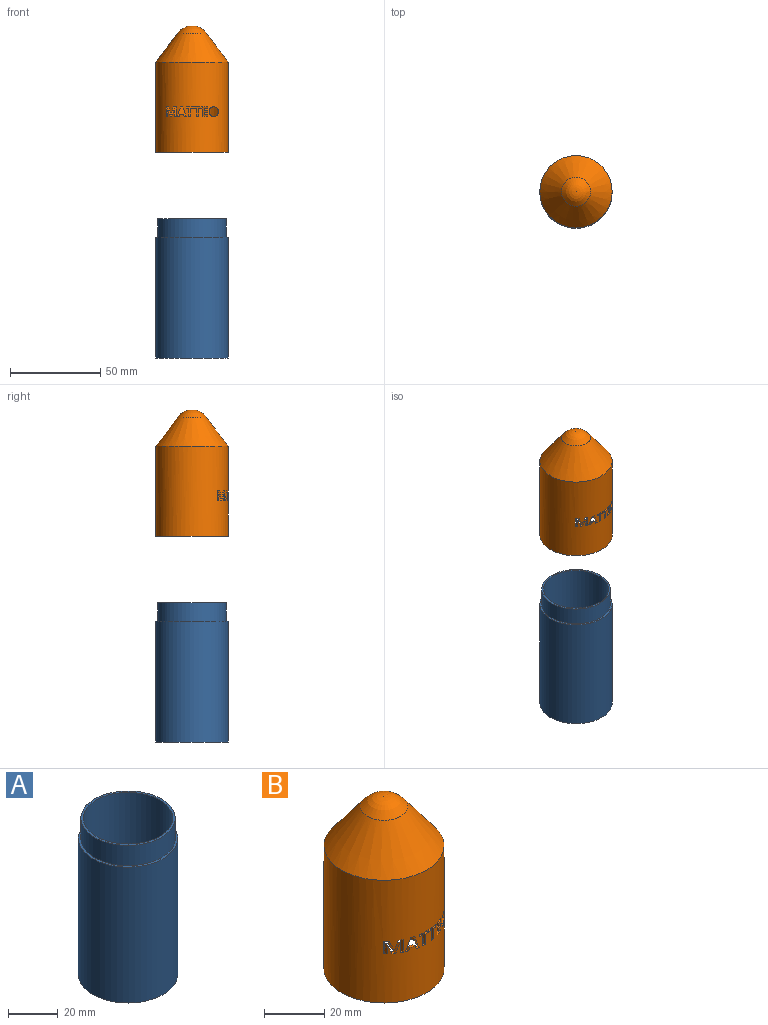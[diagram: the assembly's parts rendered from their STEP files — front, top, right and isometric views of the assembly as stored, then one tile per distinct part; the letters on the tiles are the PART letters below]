
ASSEMBLY  parts=2 mates=1
PART A: 7 faces, bbox 40x40x77 mm
  f0: plane 38x38mm, normal (0,0,1), area 116.2mm2, adj f1,f3
  f1: cylinder r=18mm len=75mm, axis (0,0,-1), area 8482.3mm2, adj f0,f2
  f2: plane 36x36mm, normal (0,0,1), area 1017.9mm2, adj f1
  f3: cylinder r=19mm len=38mm, axis (0,0,1), area 1193.8mm2, adj f0,f4
  f4: plane 40x40mm, normal (0,0,1), area 122.5mm2, adj f3,f6
  f5: plane 40x40mm, normal (0,0,-1), area 1256.6mm2, adj f6
  f6: cylinder r=20mm len=67mm, axis (0,0,-1), area 8419.5mm2, adj f4,f5
PART B: 69 faces, bbox 40x40x70 mm
  f0: cylinder r=19mm len=50mm, axis (0,0,-1), area 5875mm2, adj f2,f3,f6,f7,f8,f9,f10,f11
  f1: cylinder r=20mm len=50mm, axis (0,0,-1), area 6191.1mm2, adj f2,f4,f6,f7,f8,f9,f10,f11
  f2: plane 40x40mm, normal (0,0,-1), area 122.5mm2, adj f0,f1
  f3: plane 38x38mm, normal (0,0,-1), area 1134.1mm2, adj f0
  f4: cone r=20mm half-angle=36.9deg, axis (0,0,-1), area 1759.3mm2, adj f1,f5
  f5: revolved ~16x16mm, area 252.6mm2, adj f4
  f6: extruded ~2.14x1.97mm, area 3.1mm2, adj f0,f1,f7,f13
  f7: extruded ~2.99x1.82mm, area 2.7mm2, adj f0,f1,f6,f8
  f8: extruded ~2.5x1.82mm, area 2.5mm2, adj f0,f1,f7,f9
  f9: extruded ~1.98x1.54mm, area 2.5mm2, adj f0,f1,f8,f10
  f10: extruded ~1.97x1.54mm, area 2.5mm2, adj f0,f1,f9,f11
  f11: extruded ~2.51x1.83mm, area 2.5mm2, adj f0,f1,f10,f12
  f12: extruded ~2.99x1.82mm, area 2.7mm2, adj f0,f1,f11,f13
  f13: extruded ~2.14x1.97mm, area 3.1mm2, adj f0,f1,f6,f12
  f14: plane 4.25x1mm, normal (-1,0,0), area 4.2mm2, adj f0,f1,f15,f21
  f15: plane 1.4x1.02mm, normal (0,0,1), area 1.4mm2, adj f0,f1,f14,f16
  f16: plane 1x0.91mm, normal (-1,0,0), area 0.9mm2, adj f0,f1,f15,f17
  f17: plane 3.89x1.25mm, normal (0,0,-1), area 3.9mm2, adj f0,f1,f16,f18
  f18: plane 1.01x0.91mm, normal (1,0,0), area 0.9mm2, adj f0,f1,f17,f19
  f19: plane 1.4x1.18mm, normal (0,0,1), area 1.4mm2, adj f0,f1,f18,f20
  f20: plane 4.25x1mm, normal (1,0,0), area 4.3mm2, adj f0,f1,f19,f21
  f21: plane 1.09x1.06mm, normal (0,0,1), area 1.1mm2, adj f0,f1,f14,f20
  f22: plane 4.25x1.02mm, normal (-1,0,0), area 4.3mm2, adj f0,f1,f23,f29
  f23: plane 1.4x1.34mm, normal (0,0,1), area 1.4mm2, adj f0,f1,f22,f24
  f24: plane 1.04x0.91mm, normal (-1,0,0), area 0.9mm2, adj f0,f1,f23,f25
  f25: plane 3.89x1.64mm, normal (0,0,-1), area 3.9mm2, adj f0,f1,f24,f26
  f26: plane 1x0.91mm, normal (1,0,0), area 0.9mm2, adj f0,f1,f25,f27
  f27: plane 1.4x1.14mm, normal (0,0,1), area 1.4mm2, adj f0,f1,f26,f28
  f28: plane 4.25x1.01mm, normal (1,0,0), area 4.3mm2, adj f0,f1,f27,f29
  f29: plane 1.19x1.09mm, normal (0,0,1), area 1.1mm2, adj f0,f1,f22,f28
  f30: plane 1.12x0.9mm, normal (-1,0,0), area 1mm2, adj f0,f1,f31,f41
  f31: plane 1.92x1.88mm, normal (0,0,-1), area 2.1mm2, adj f0,f1,f30,f32
  f32: plane 1.33x1.07mm, normal (-1,0,0), area 1.4mm2, adj f0,f1,f31,f33
  f33: plane 1.85x1.75mm, normal (0,0,1), area 1.9mm2, adj f0,f1,f32,f34
  f34: plane 1.12x0.9mm, normal (-1,0,0), area 1mm2, adj f0,f1,f33,f35
  f35: plane 1.85x1.75mm, normal (0,0,-1), area 1.9mm2, adj f0,f1,f34,f36
  f36: plane 1.13x1.07mm, normal (-1,0,0), area 1.2mm2, adj f0,f1,f35,f37
  f37: plane 1.92x1.88mm, normal (0,0,1), area 2.1mm2, adj f0,f1,f36,f38
  f38: plane 1.12x0.9mm, normal (-1,0,0), area 1mm2, adj f0,f1,f37,f39
  f39: plane 2.97x2.29mm, normal (0,0,-1), area 3.2mm2, adj f0,f1,f38,f40
  f40: plane 5.16x1.05mm, normal (1,0,0), area 5.4mm2, adj f0,f1,f39,f41
  f41: plane 2.97x2.29mm, normal (0,0,1), area 3.2mm2, adj f0,f1,f30,f40
  f42: plane 1.23x1.12mm, normal (0.96,0,0.29), area 1.3mm2, adj f0,f1,f43,f49
  f43: plane 1.88x1.62mm, normal (0,0,1), area 2mm2, adj f0,f1,f42,f44
  f44: plane 1.23x1.21mm, normal (-0.96,0,0.29), area 1.4mm2, adj f0,f1,f43,f45
  f45: plane 1.59x1.18mm, normal (0,0,1), area 1.3mm2, adj f0,f1,f44,f46
  f46: plane 5.18x1.82mm, normal (0.94,0,-0.33), area 5.9mm2, adj f0,f1,f45,f47
  f47: plane 1.46x1.34mm, normal (0,0,-1), area 1.4mm2, adj f0,f1,f46,f48
  f48: plane 5.2x1.85mm, normal (-0.94,0,-0.33), area 5.6mm2, adj f0,f1,f47,f49
  f49: plane 1.25x1.18mm, normal (0,0,1), area 1.2mm2, adj f0,f1,f42,f48
  f50: plane 2x1mm, normal (0,0,1), area 1.3mm2, adj f0,f1,f51,f68
  f51: plane 4.04x2.04mm, normal (-0.95,0,0.31), area 5mm2, adj f0,f1,f50,f52
  f52: plane 1.18x0.03mm, normal (0,0,1), area 0mm2, adj f0,f1,f51,f53
  f53: extruded ~1.2x1.19mm, area 1.4mm2, adj f0,f1,f52,f54
  f54: extruded ~1.16x0.4mm, area 0.5mm2, adj f0,f1,f53,f55
  f55: plane 2.44x1.16mm, normal (1,0,0), area 2.8mm2, adj f0,f1,f54,f56
  f56: plane 1.7x1.02mm, normal (0,0,1), area 1.2mm2, adj f0,f1,f55,f57
  f57: plane 5.16x1.12mm, normal (-1,0,0), area 5.8mm2, adj f0,f1,f56,f58
  f58: plane 1.99x1.49mm, normal (0,0,-1), area 1.7mm2, adj f0,f1,f57,f59
  f59: plane 3.94x2.1mm, normal (0.95,0,-0.31), area 5mm2, adj f0,f1,f58,f60
  f60: plane 1.26x0.02mm, normal (0,0,-1), area 0mm2, adj f0,f1,f59,f61
  f61: plane 3.94x2.28mm, normal (-0.96,0,-0.3), area 5.3mm2, adj f0,f1,f60,f62
  f62: plane 2.86x1.49mm, normal (0,0,-1), area 2.1mm2, adj f0,f1,f61,f63
  f63: plane 5.16x1.48mm, normal (1,0,0), area 7.6mm2, adj f0,f1,f62,f64
  f64: plane 2.42x0.98mm, normal (0,0,1), area 1.4mm2, adj f0,f1,f63,f65
  f65: plane 2.4x1.38mm, normal (-1,0,0), area 3.3mm2, adj f0,f1,f64,f66
  f66: extruded ~1.65x1.44mm, area 2.3mm2, adj f0,f1,f65,f67
  f67: plane 1.41x0.03mm, normal (0,0,1), area 0mm2, adj f0,f1,f66,f68
  f68: plane 4.04x2.41mm, normal (0.96,0,0.29), area 5.6mm2, adj f0,f1,f50,f67
PLACE A t=(0.78,-1.39,-0.5)mm fixed
PLACE B t=(0.78,-1.39,113.39)mm
MATE slider B.f0 <-> A.f1  axis (0,0,-1) through (0.78,-1.39,113.39)mm
